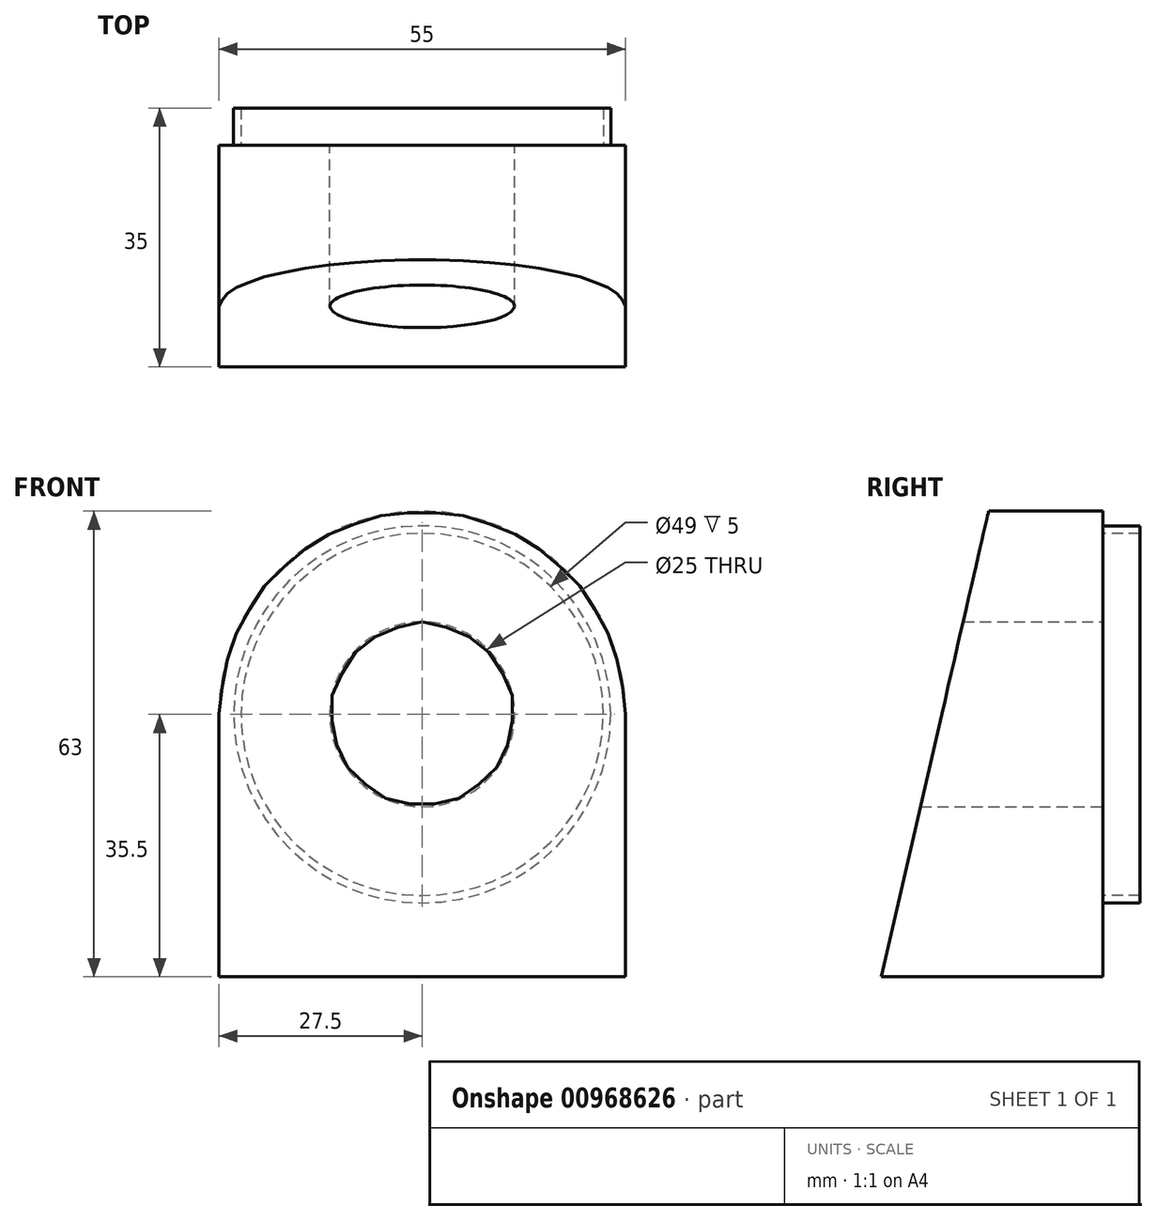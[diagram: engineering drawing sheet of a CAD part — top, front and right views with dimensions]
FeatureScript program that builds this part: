
annotation { "Feature Type Name" : "Feature", "Feature Type Description" : "" }
export const myFeature = defineFeature(function(context is Context, id is Id, definition is map)
    precondition{}
    {
        {
            var Q0;
            Q0=qCreatedBy(makeId("Front.planeOp"),FACE);
            var sketch = newSketch(context, id + "F0", { "sketchPlane" : qUnion([Q0])});
            skCircle(sketch, "E0", {"center": v(0, 35.5) * mm, "radius": 25 * mm, "construction": true});
            skCircle(sketch, "E1", {"center": v(0, 35.5) * mm, "radius": 24.5 * mm});
            skCircle(sketch, "E2", {"center": v(0, 35.5) * mm, "radius": 25.5 * mm});
            skSolve(sketch);
        }
        {
            var Q0;
            Q0 = qSketchRegion(id + "F0", true);
            extrude(context, id + "F1", {"entities" : qUnion([Q0]), "oppositeDirection" : true, "depth" : 5 * mm, "offsetDistance" : 25 * mm});
        }
        {
            var Q0;
            Q0=qCreatedBy(makeId("Right.planeOp"),FACE);
            var sketch = newSketch(context, id + "F2", { "sketchPlane" : qUnion([Q0])});
            skLineSegment(sketch, "E3", {"start": v(0, 0) * mm, "end": v(-30, 0) * mm});
            skLineSegment(sketch, "E4", {"start": v(-30, 0) * mm, "end": v(-15, 65) * mm});
            skLineSegment(sketch, "E5", {"start": v(-15, 65) * mm, "end": v(0, 65) * mm});
            skLineSegment(sketch, "E6", {"start": v(0, 65) * mm, "end": v(0, 0) * mm});
            skSolve(sketch);
        }
        {
            var Q0;
            Q0=makeQuery(id+"F2.imprint","IMPRINT",FACE,{"disambiguationData":[TD([[makeQuery(id+"F2.imprint","IMPRINT",EDGE,{"derivedFrom":sQuery(id+"F2.wireOp",EDGE,"E3")}),-1.0]])]});
            extrude(context, id + "F3", {"entities" : qUnion([Q0]), "operationType" : NewBodyOperationType.ADD, "endBound" : BoundingType.SYMMETRIC, "depth" : (50 + 1 + 4) * mm, "offsetDistance" : 25 * mm});
        }
        {
            var Q0;
            Q0=qCreatedBy(makeId("Front.planeOp"),FACE);
            var sketch = newSketch(context, id + "F4", { "sketchPlane" : qUnion([Q0])});
            skArc(sketch, "E7", {"start": v(27.5, 35.5) * mm, "mid": v(0, 63) * mm, "end": v(-27.5, 35.5) * mm});
            skLineSegment(sketch, "E8", {"start": v(27.5, 35.5) * mm, "end": v(32.5, 35.5) * mm});
            skLineSegment(sketch, "E9", {"start": v(32.5, 35.5) * mm, "end": v(32.5, 70) * mm});
            skLineSegment(sketch, "E10", {"start": v(32.5, 70) * mm, "end": v(-32.5, 70) * mm});
            skLineSegment(sketch, "E11", {"start": v(-32.5, 70) * mm, "end": v(-32.5, 35.5) * mm});
            skLineSegment(sketch, "E12", {"start": v(-32.5, 35.5) * mm, "end": v(-27.5, 35.5) * mm});
            skCircle(sketch, "E13", {"center": v(0, 35.5) * mm, "radius": 12.5 * mm});
            skSolve(sketch);
        }
        {
            var Q0;
            Q0=makeQuery(id+"F4.imprint","IMPRINT",FACE,{"disambiguationData":[TD([[makeQuery(id+"F4.imprint","IMPRINT",EDGE,{"derivedFrom":sQuery(id+"F4.wireOp",EDGE,"E7")}),-1.0]])]});
            var Q1;
            Q1=makeQuery(id+"F4.imprint","IMPRINT",FACE,{"disambiguationData":[TD([[makeQuery(id+"F4.imprint","IMPRINT",EDGE,{"derivedFrom":sQuery(id+"F4.wireOp",EDGE,"E13")}),1.0]])]});
            extrude(context, id + "F5", {"entities" : qUnion([Q0, Q1]), "operationType" : NewBodyOperationType.REMOVE, "endBound" : BoundingType.THROUGH_ALL, "depth" : 25 * mm, "offsetDistance" : 25 * mm});
        }
    });
